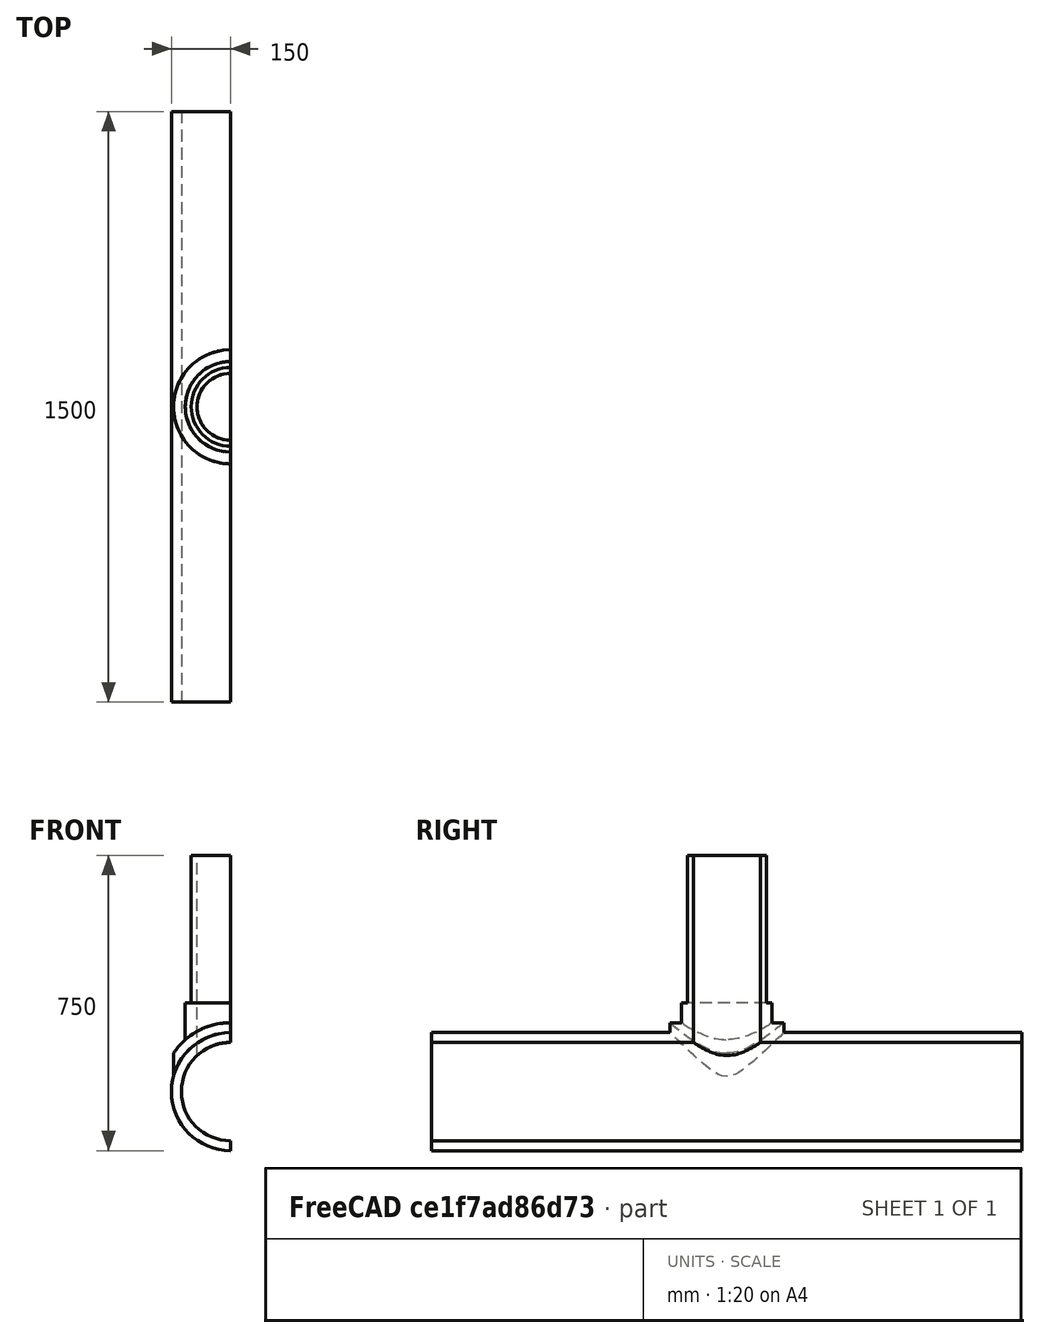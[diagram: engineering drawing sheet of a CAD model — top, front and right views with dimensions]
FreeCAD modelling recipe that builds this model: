
FCSTD DOCUMENT  (FreeCAD 0.16RUnknown)
Label: T-pipe CAD
License: All rights reserved
LicenseURL: http://en.wikipedia.org/wiki/All_rights_reserved
objects: Part::Cylinder×8, Part::Cut×6, Part::Box×2, Part::MultiFuse×1
note: 17 computed .brp shape members not serialized (recipe doc carries the construction recipe); baked Part::Feature solids carry a one-line shape summary decoded from their .brp

FEATURE [Part::Cylinder] Cylinder
  Angle = 360
  Height = 600
  Radius = 100
FEATURE [Part::Cylinder] Cylinder001
  Angle = 360
  Height = 1500
  Placement = pos=(0,750,0) rot=(1,0,0;1.5708rad)
  Radius = 150
FEATURE [Part::Cylinder] Cylinder002
  Angle = 360
  Height = 225
  Radius = 115
FEATURE [Part::Cylinder] Cylinder003
  Angle = 360
  Height = 400
  Placement = pos=(0,200,0) rot=(1,0,0;1.5708rad)
  Radius = 175
FEATURE [Part::Cylinder] Cylinder004
  Angle = 360
  Height = 600
  Radius = 145
FEATURE [Part::Cylinder] Cylinder005
  Angle = 360
  Height = 600
  Radius = 300
FEATURE [Part::Cut] Cut
  Base = -> Cylinder005
  Tool = -> Cylinder004
FEATURE [Part::Cut] Cut001
  Base = -> Cylinder003
  Tool = -> Cut
FEATURE [Part::Box] Box  label="Cube"
  Height = 500
  Length = 500
  Placement = pos=(-226,-279,-480) rot=(0,0,1;0rad)
  Width = 500
FEATURE [Part::Cut] Cut002
  Base = -> Cut001
  Tool = -> Box
FEATURE [Part::MultiFuse] Fusion
  Shapes = -> [Cut002,Cylinder002,Cylinder001,Cylinder]
FEATURE [Part::Cylinder] Cylinder006
  Angle = 360
  Height = 600
  Radius = 85
FEATURE [Part::Cut] Cut003
  Base = -> Fusion
  Tool = -> Cylinder006
FEATURE [Part::Cylinder] Cylinder007
  Angle = 360
  Height = 1500
  Placement = pos=(0,750,0) rot=(1,0,0;1.5708rad)
  Radius = 125
FEATURE [Part::Cut] Cut004
  Base = -> Cut003
  Tool = -> Cylinder007
FEATURE [Part::Box] Box001  label="Cube001"
  Height = 2000
  Length = 2000
  Placement = pos=(0,-1000,-1000) rot=(0,0,1;0rad)
  Width = 2000
FEATURE [Part::Cut] Cut005
  Base = -> Cut004
  Tool = -> Box001
